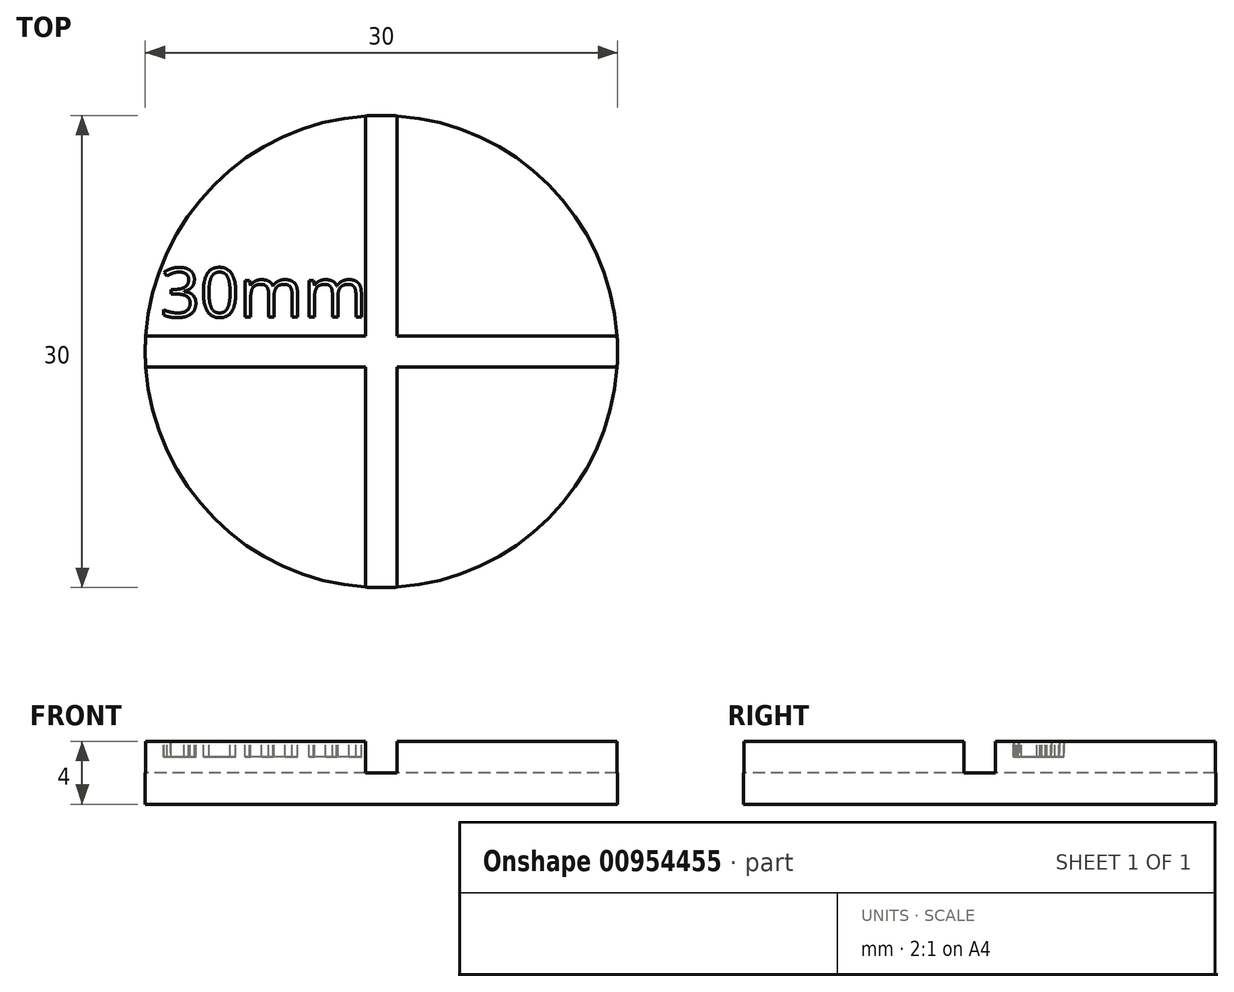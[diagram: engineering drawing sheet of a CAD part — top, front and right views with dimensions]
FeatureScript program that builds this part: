
annotation { "Feature Type Name" : "Feature", "Feature Type Description" : "" }
export const myFeature = defineFeature(function(context is Context, id is Id, definition is map)
    precondition{}
    {
        {
            var Q0;
            Q0=qCreatedBy(makeId("Top.planeOp"),FACE);
            var sketch = newSketch(context, id + "F0", { "sketchPlane" : qUnion([Q0])});
            skCircle(sketch, "E0", {"center": v(0, 0) * mm, "radius": 15 * mm});
            skSolve(sketch);
        }
        {
            var Q0;
            Q0 = qSketchRegion(id + "F0", true);
            extrude(context, id + "F1", {"entities" : qUnion([Q0]), "depth" : 4 * mm, "offsetDistance" : 25 * mm});
        }
        {
            var Q0;
            Q0=makeQuery(id+"F1.opExtrude","CAP_FACE",FACE,{"disambiguationData":[OSD([sQuery(id+"F0.wireOp",EDGE,"E0")])],"isStart":false});
            var sketch = newSketch(context, id + "F2", { "sketchPlane" : qUnion([Q0])});
            skLineSegment(sketch, "E1.bottom", {"start": v(24.69, -1) * mm, "end": v(-24.69, -1) * mm});
            skLineSegment(sketch, "E1.top", {"start": v(24.69, 1) * mm, "end": v(-24.69, 1) * mm});
            skLineSegment(sketch, "E1.left", {"start": v(24.69, -1) * mm, "end": v(24.69, 1) * mm});
            skLineSegment(sketch, "E1.right", {"start": v(-24.69, -1) * mm, "end": v(-24.69, 1) * mm});
            skPoint(sketch, "E1.middle", {"position": v(0, 0) * mm});
            skLineSegment(sketch, "E2.bottom", {"start": v(-1, 17.63) * mm, "end": v(1, 17.63) * mm});
            skLineSegment(sketch, "E2.top", {"start": v(-1, -17.63) * mm, "end": v(1, -17.63) * mm});
            skLineSegment(sketch, "E2.left", {"start": v(-1, 17.63) * mm, "end": v(-1, -17.63) * mm});
            skLineSegment(sketch, "E2.right", {"start": v(1, 17.63) * mm, "end": v(1, -17.63) * mm});
            skSolve(sketch);
        }
        {
            var Q0;
            Q0 = qSketchRegion(id + "F2", true);
            extrude(context, id + "F3", {"entities" : qUnion([Q0]), "operationType" : NewBodyOperationType.REMOVE, "oppositeDirection" : true, "depth" : 2 * mm, "offsetDistance" : 25 * mm});
        }
        {
            var Q0;
            {var subQ0=sQuery(id+"F0.wireOp",EDGE,"E0");var subQ1=sQuery(id+"F2.wireOp",EDGE,"E1.top");var subQ4=sQuery(id+"F2.wireOp",EDGE,"E2.left");var subQ5=makeQuery(id+"F2.imprint","INTERSECT",VERTEX,{"derivedFrom":[subQ1,subQ4]});Q0=makeQuery(id+"F3.boolean.opBoolean","SPLIT",FACE,{"disambiguationData":[TD([makeQuery(id+"F3.opExtrude","SWEPT_FACE",FACE,{"disambiguationData":[OSD([subQ1]),TDD([makeQuery(id+"F2.imprint","IMPRINT",EDGE,{"disambiguationData":[TD([[subQ5,-1.0]])],"derivedFrom":subQ1}),makeQuery(id+"F2.imprint","IMPRINT",EDGE,{"disambiguationData":[TD([[makeQuery(id+"F2.imprint","INTERSECT",VERTEX,{"derivedFrom":[subQ1,sQuery(id+"F2.wireOp",EDGE,"E1.right")]}),1.0]])],"derivedFrom":subQ1})])]})])],"derivedFrom":makeQuery(id+"F1.opExtrude","CAP_FACE",FACE,{"disambiguationData":[OSD([subQ0])],"isStart":false})});}
            var sketch = newSketch(context, id + "F4", { "sketchPlane" : qUnion([Q0])});
            skText(sketch, "E3", { "text": "30mm", "fontName": "OpenSans-Regular.ttf"});
            const initialGuessF4  = {"E3": [-0.01402, 0.00219, 1, 0, 0.00314]};
            skSetInitialGuess(sketch, initialGuessF4);
            skSolve(sketch);
        }
        {
            var Q0;
            Q0 = qSketchRegion(id + "F4", true);
            extrude(context, id + "F5", {"entities" : qUnion([Q0]), "operationType" : NewBodyOperationType.REMOVE, "oppositeDirection" : true, "depth" : 1 * mm, "offsetDistance" : 25 * mm});
        }
    });
